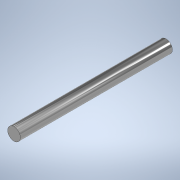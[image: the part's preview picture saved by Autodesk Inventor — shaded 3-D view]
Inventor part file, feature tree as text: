
AUTODESK INVENTOR PART (.ipt)
format: ipt  version: 2021 (Build 250183000, 183)  size: 96,256 bytes
history: native  units: mm
features: other x1, extrude x1, sketch x1
ambient origin geometry x8: Origin, YZ Plane, XZ Plane, XY Plane, X Axis, Y Axis, Z Axis, Center Point
bodies: Body1 (feature_tree)
feature tree (3):
  other  "Sólido1"
  extrude  "Extrusão1"  Depth=6.0mm TaperAngle=0.0deg
  sketch  "Esboço1"  dims[d0=0.5mm d1=6.0mm d2=0.0mm]
